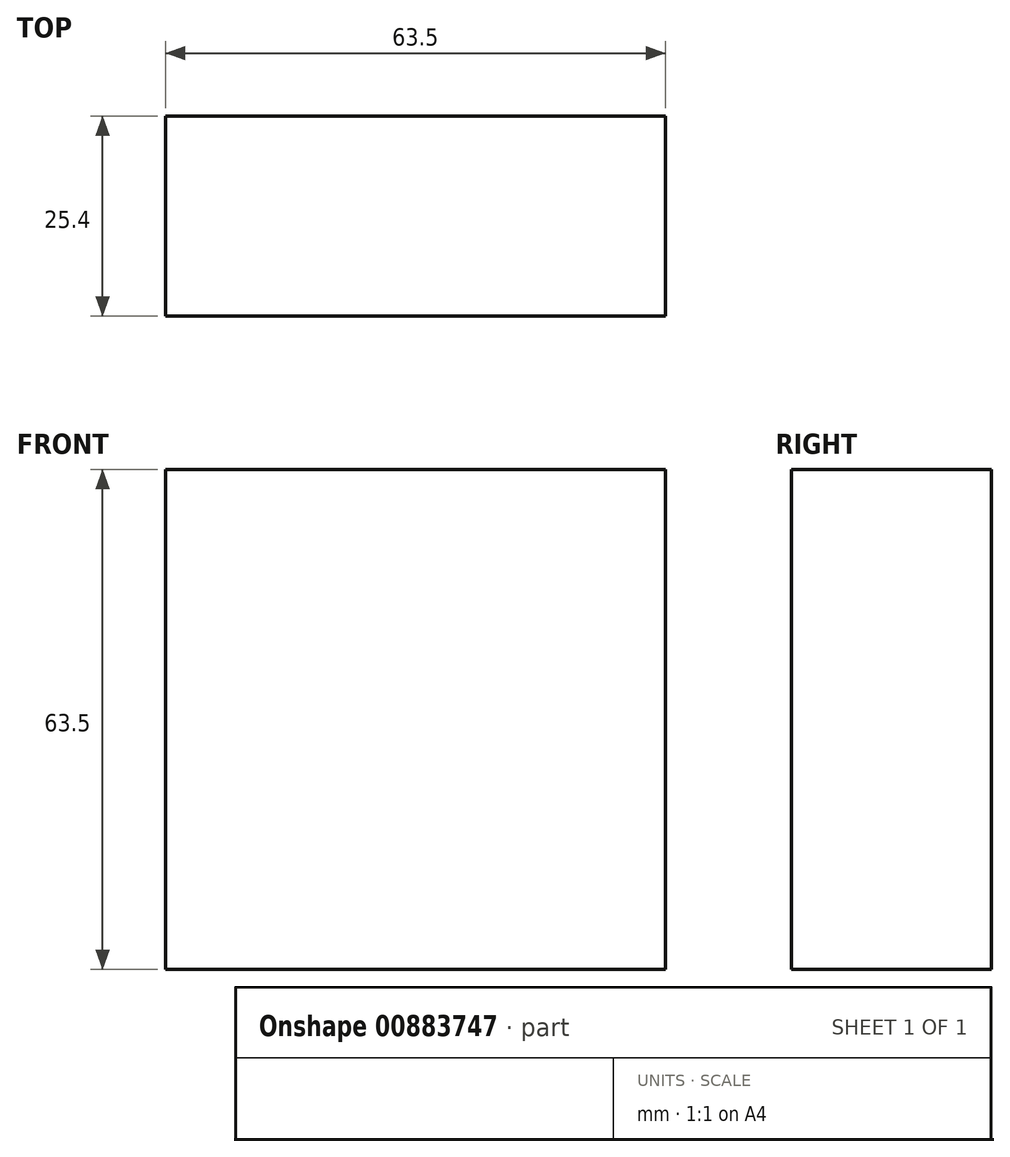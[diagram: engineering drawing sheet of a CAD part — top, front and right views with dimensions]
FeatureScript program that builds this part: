
annotation { "Feature Type Name" : "Feature", "Feature Type Description" : "" }
export const myFeature = defineFeature(function(context is Context, id is Id, definition is map)
    precondition{}
    {
        {
            var Q0;
            Q0=qCreatedBy(makeId("Front.planeOp"),FACE);
            var sketch = newSketch(context, id + "F0", { "sketchPlane" : qUnion([Q0])});
            skLineSegment(sketch, "E0.bottom", {"start": v(31.75, 31.75) * mm, "end": v(-31.75, 31.75) * mm});
            skLineSegment(sketch, "E0.top", {"start": v(31.75, -31.75) * mm, "end": v(-31.75, -31.75) * mm});
            skLineSegment(sketch, "E0.left", {"start": v(31.75, 31.75) * mm, "end": v(31.75, -31.75) * mm});
            skLineSegment(sketch, "E0.right", {"start": v(-31.75, 31.75) * mm, "end": v(-31.75, -31.75) * mm});
            skPoint(sketch, "E0.middle", {"position": v(0, 0) * mm});
            skSolve(sketch);
        }
        {
            var Q0;
            Q0 = qSketchRegion(id + "F0", true);
            extrude(context, id + "F1", {"entities" : qUnion([Q0]), "depth" : 25.4 * mm, "offsetDistance" : 25.4 * mm});
        }
    });
